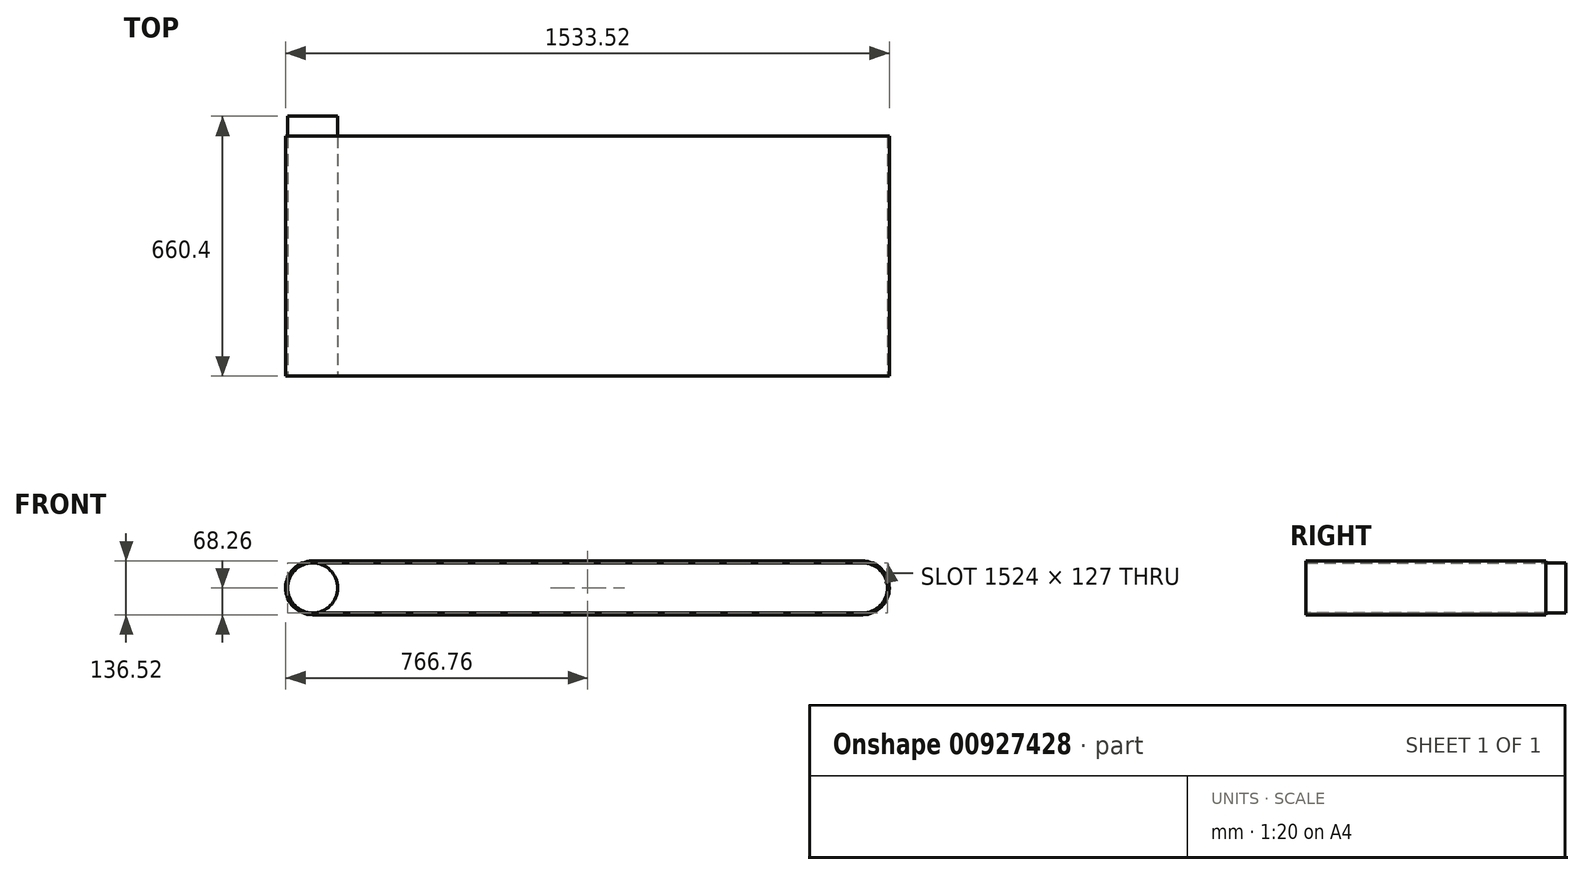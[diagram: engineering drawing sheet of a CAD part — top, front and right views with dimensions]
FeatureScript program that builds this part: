
annotation { "Feature Type Name" : "Feature", "Feature Type Description" : "" }
export const myFeature = defineFeature(function(context is Context, id is Id, definition is map)
    precondition{}
    {
        {
            var Q0;
            Q0=qCreatedBy(makeId("Front.planeOp"),FACE);
            var sketch = newSketch(context, id + "F0", { "sketchPlane" : qUnion([Q0])});
            skLineSegment(sketch, "E0", {"start": v(0, 0) * mm, "end": v(1397, 0) * mm, "construction": true});
            skLineSegment(sketch, "E1", {"start": v(1397, 63.5) * mm, "end": v(0, 63.5) * mm});
            skLineSegment(sketch, "E2", {"start": v(0, -63.5) * mm, "end": v(1397, -63.5) * mm});
            skArc(sketch, "E3", {"start": v(0, 63.5) * mm, "mid": v(-63.5, 0) * mm, "end": v(0, -63.5) * mm});
            skArc(sketch, "E4", {"start": v(0, -63.5) * mm, "mid": v(63.5, 0) * mm, "end": v(0, 63.5) * mm});
            skArc(sketch, "E5", {"start": v(1397, 63.5) * mm, "mid": v(1333.5, 0) * mm, "end": v(1397, -63.5) * mm});
            skArc(sketch, "E6", {"start": v(1397, -63.5) * mm, "mid": v(1460.5, 0) * mm, "end": v(1397, 63.5) * mm});
            skSolve(sketch);
        }
        {
            var Q0;
            Q0=sQuery(id+"F0.wireOp",VERTEX,"E1.start");
            var Q1;
            Q1=sQuery(id+"F0.wireOp",EDGE,"E1");
            cPlane(context, id + "F1", {"entities" : qUnion([Q0, Q1]), "cplaneType" : CPlaneType.LINE_POINT, "offset" : 25.4 * mm, "width" : 152.4 * mm, "height" : 152.4 * mm});
        }
        {
            var Q0;
            Q0=qCreatedBy(id+"F1.planeOp",FACE);
            var sketch = newSketch(context, id + "F2", { "sketchPlane" : qUnion([Q0])});
            skLineSegment(sketch, "E7", {"start": v(0, 63.5) * mm, "end": v(-609.6, 63.5) * mm});
            skLineSegment(sketch, "E8", {"start": v(-609.6, 63.5) * mm, "end": v(-609.6, 68.26) * mm});
            skLineSegment(sketch, "E9", {"start": v(-609.6, 68.26) * mm, "end": v(0, 68.26) * mm});
            skLineSegment(sketch, "E10", {"start": v(0, 68.26) * mm, "end": v(0, 63.5) * mm});
            skSolve(sketch);
        }
        {
            var Q0;
            Q0=makeQuery(id+"F2.imprint","IMPRINT",FACE,{"disambiguationData":[TD([[makeQuery(id+"F2.imprint","IMPRINT",EDGE,{"derivedFrom":sQuery(id+"F2.wireOp",EDGE,"E7")}),-1.0]])]});
            var Q1;
            Q1=sQuery(id+"F0.wireOp",EDGE,"E1");
            var Q2;
            Q2=sQuery(id+"F0.wireOp",EDGE,"E3");
            var Q3;
            Q3=sQuery(id+"F0.wireOp",EDGE,"E2");
            var Q4;
            Q4=sQuery(id+"F0.wireOp",EDGE,"E6");
            sweep(context, id + "F3", {"profiles" : qUnion([Q0]), "path" : qUnion([Q1, Q2, Q3, Q4])});
        }
        {
            var Q0;
            Q0=makeQuery(id+"F0.imprint","IMPRINT",FACE,{"disambiguationData":[TD([[makeQuery(id+"F0.imprint","IMPRINT",EDGE,{"derivedFrom":sQuery(id+"F0.wireOp",EDGE,"E3")}),1.0]])]});
            extrude(context, id + "F4", {"entities" : qUnion([Q0]), "oppositeDirection" : true, "depth" : 660.4 * mm, "offsetDistance" : 25.4 * mm});
        }
    });
